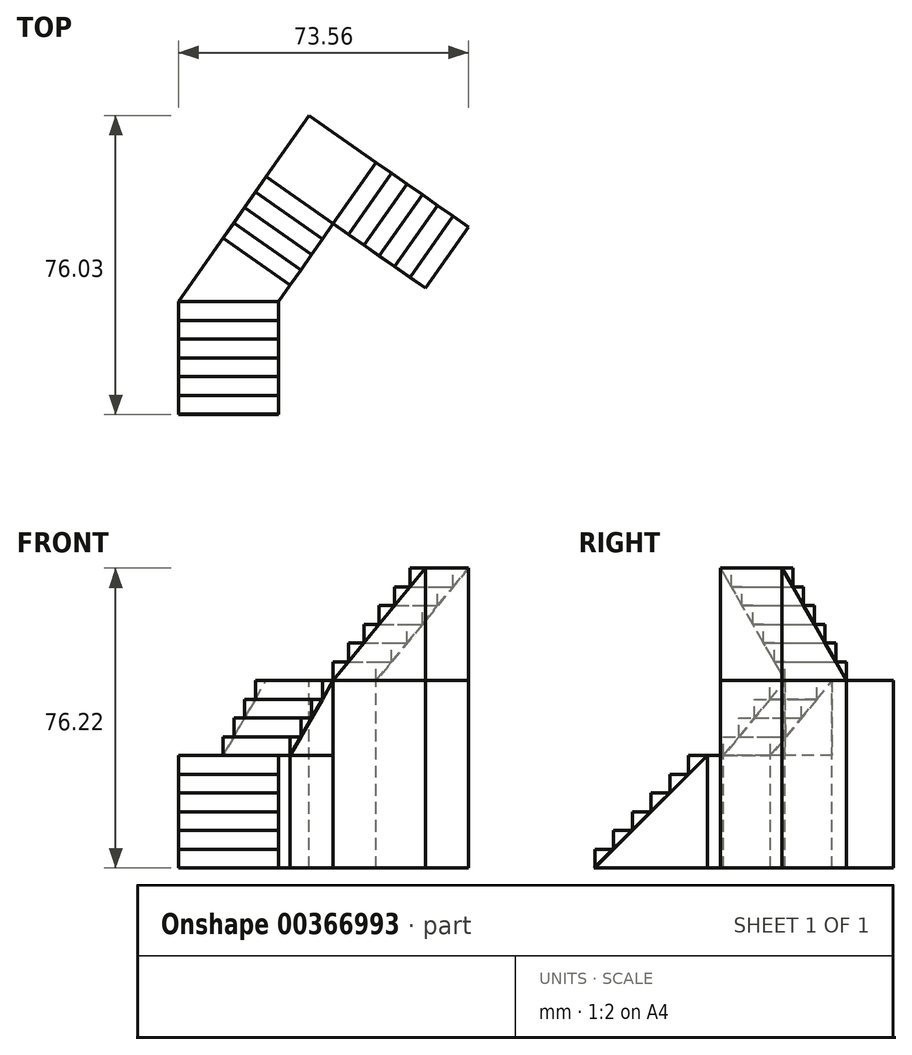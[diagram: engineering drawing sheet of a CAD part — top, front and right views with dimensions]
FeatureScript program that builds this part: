
annotation { "Feature Type Name" : "Feature", "Feature Type Description" : "" }
export const myFeature = defineFeature(function(context is Context, id is Id, definition is map)
    precondition{}
    {
        {
            var Q0;
            Q0=qCreatedBy(makeId("Right.planeOp"),FACE);
            var sketch = newSketch(context, id + "F0", { "sketchPlane" : qUnion([Q0])});
            skLineSegment(sketch, "E0", {"start": v(-19.36, -10.94) * mm, "end": v(9.22, 17.63) * mm});
            skLineSegment(sketch, "E1", {"start": v(-19.36, -10.94) * mm, "end": v(-19.36, -6.18) * mm});
            skLineSegment(sketch, "E2", {"start": v(-19.36, -6.18) * mm, "end": v(-14.6, -6.18) * mm});
            skLineSegment(sketch, "E3", {"start": v(-19.36, -10.94) * mm, "end": v(28.85, -10.94) * mm});
            skLineSegment(sketch, "E4", {"start": v(-14.6, -6.18) * mm, "end": v(-14.6, -1.42) * mm});
            skLineSegment(sketch, "E5", {"start": v(-14.6, -1.42) * mm, "end": v(-9.83, -1.42) * mm});
            skLineSegment(sketch, "E6", {"start": v(-9.83, -1.42) * mm, "end": v(-9.83, 3.35) * mm});
            skLineSegment(sketch, "E7", {"start": v(-9.83, 3.35) * mm, "end": v(-5.07, 3.35) * mm});
            skLineSegment(sketch, "E8", {"start": v(-5.07, 3.35) * mm, "end": v(-5.07, 8.1) * mm});
            skLineSegment(sketch, "E9", {"start": v(-5.07, 8.1) * mm, "end": v(-0.3, 8.1) * mm});
            skLineSegment(sketch, "E10", {"start": v(-0.3, 8.1) * mm, "end": v(-0.3, 12.87) * mm});
            skLineSegment(sketch, "E11", {"start": v(-0.3, 12.87) * mm, "end": v(4.45, 12.87) * mm});
            skLineSegment(sketch, "E12", {"start": v(4.45, 12.87) * mm, "end": v(4.45, 17.63) * mm});
            skLineSegment(sketch, "E13", {"start": v(4.45, 17.63) * mm, "end": v(9.22, 17.63) * mm});
            skSolve(sketch);
        }
        {
            var Q0;
            {var subQ2=sQuery(id+"F0.wireOp",EDGE,"E12");Q0=makeQuery(id+"F0.imprint","IMPRINT",FACE,{"disambiguationData":[TD([[makeQuery(id+"F0.imprint","IMPRINT",EDGE,{"derivedFrom":subQ2}),-1.0]])]});}
            var Q1;
            {var subQ0=sQuery(id+"F0.wireOp",EDGE,"E10");Q1=makeQuery(id+"F0.imprint","IMPRINT",FACE,{"disambiguationData":[TD([[makeQuery(id+"F0.imprint","IMPRINT",EDGE,{"derivedFrom":subQ0}),-1.0]])]});}
            var Q2;
            {var subQ0=sQuery(id+"F0.wireOp",EDGE,"E8");Q2=makeQuery(id+"F0.imprint","IMPRINT",FACE,{"disambiguationData":[TD([[makeQuery(id+"F0.imprint","IMPRINT",EDGE,{"derivedFrom":subQ0}),-1.0]])]});}
            var Q3;
            {var subQ0=sQuery(id+"F0.wireOp",EDGE,"E6");Q3=makeQuery(id+"F0.imprint","IMPRINT",FACE,{"disambiguationData":[TD([[makeQuery(id+"F0.imprint","IMPRINT",EDGE,{"derivedFrom":subQ0}),-1.0]])]});}
            var Q4;
            {var subQ0=sQuery(id+"F0.wireOp",EDGE,"E4");Q4=makeQuery(id+"F0.imprint","IMPRINT",FACE,{"disambiguationData":[TD([[makeQuery(id+"F0.imprint","IMPRINT",EDGE,{"derivedFrom":subQ0}),-1.0]])]});}
            var Q5;
            {var subQ0=sQuery(id+"F0.wireOp",EDGE,"E1");Q5=makeQuery(id+"F0.imprint","IMPRINT",FACE,{"disambiguationData":[TD([[makeQuery(id+"F0.imprint","IMPRINT",EDGE,{"derivedFrom":subQ0}),-1.0]])]});}
            extrude(context, id + "F1", {"entities" : qUnion([Q0, Q1, Q2, Q3, Q4, Q5]), "depth" : 25.4 * mm});
        }
        {
            var Q0;
            Q0=makeQuery(id+"F1.opExtrude","SWEPT_FACE",FACE,{"disambiguationData":[OSD([sQuery(id+"F0.wireOp",EDGE,"E13")])]});
            var sketch = newSketch(context, id + "F2", { "sketchPlane" : qUnion([Q0])});
            skLineSegment(sketch, "E14", {"start": v(0, 9.22) * mm, "end": v(11.27, 25.31) * mm});
            skLineSegment(sketch, "E15", {"start": v(25.4, 9.22) * mm, "end": v(28.31, 13.38) * mm});
            skLineSegment(sketch, "E16", {"start": v(28.31, 13.38) * mm, "end": v(11.27, 25.31) * mm});
            skSolve(sketch);
        }
        {
            var Q0;
            Q0=makeQuery(id+"F2.imprint","IMPRINT",FACE,{"disambiguationData":[TD([[makeQuery(id+"F2.imprint","IMPRINT",EDGE,{"derivedFrom":sQuery(id+"F2.wireOp",EDGE,"E14")}),-1.0]])]});
            extrude(context, id + "F3", {"entities" : qUnion([Q0]), "oppositeDirection" : true, "depth" : 28.57 * mm});
        }
        {
            var Q0;
            Q0=makeQuery(id+"F3.opExtrude","SWEPT_FACE",FACE,{"disambiguationData":[OSD([sQuery(id+"F2.wireOp",EDGE,"E14")])]});
            var sketch = newSketch(context, id + "F4", { "sketchPlane" : qUnion([Q0])});
            skLineSegment(sketch, "E17", {"start": v(-27.2, 17.64) * mm, "end": v(-46.25, 36.69) * mm});
            skLineSegment(sketch, "E18", {"start": v(-27.2, 17.64) * mm, "end": v(-27.2, 22.4) * mm});
            skLineSegment(sketch, "E19", {"start": v(-27.2, 22.4) * mm, "end": v(-31.96, 22.4) * mm});
            skLineSegment(sketch, "E20", {"start": v(-31.96, 22.4) * mm, "end": v(-31.96, 27.16) * mm});
            skLineSegment(sketch, "E21", {"start": v(-31.96, 27.16) * mm, "end": v(-36.72, 27.16) * mm});
            skLineSegment(sketch, "E22", {"start": v(-36.72, 27.16) * mm, "end": v(-36.72, 31.92) * mm});
            skLineSegment(sketch, "E23", {"start": v(-36.72, 31.92) * mm, "end": v(-41.48, 31.92) * mm});
            skLineSegment(sketch, "E24", {"start": v(-41.48, 31.92) * mm, "end": v(-41.48, 36.69) * mm});
            skLineSegment(sketch, "E25", {"start": v(-41.48, 36.69) * mm, "end": v(-46.25, 36.69) * mm});
            skSolve(sketch);
        }
        {
            var Q0;
            {var subQ0=sQuery(id+"F4.wireOp",EDGE,"E20");Q0=makeQuery(id+"F4.imprint","IMPRINT",FACE,{"disambiguationData":[TD([[makeQuery(id+"F4.imprint","IMPRINT",EDGE,{"derivedFrom":subQ0}),1.0]])]});}
            var Q1;
            {var subQ0=sQuery(id+"F4.wireOp",EDGE,"E18");Q1=makeQuery(id+"F4.imprint","IMPRINT",FACE,{"disambiguationData":[TD([[makeQuery(id+"F4.imprint","IMPRINT",EDGE,{"derivedFrom":subQ0}),1.0]])]});}
            var Q2;
            {var subQ0=sQuery(id+"F4.wireOp",EDGE,"E22");Q2=makeQuery(id+"F4.imprint","IMPRINT",FACE,{"disambiguationData":[TD([[makeQuery(id+"F4.imprint","IMPRINT",EDGE,{"derivedFrom":subQ0}),1.0]])]});}
            var Q3;
            {var subQ2=sQuery(id+"F4.wireOp",EDGE,"E24");Q3=makeQuery(id+"F4.imprint","IMPRINT",FACE,{"disambiguationData":[TD([[makeQuery(id+"F4.imprint","IMPRINT",EDGE,{"derivedFrom":subQ2}),1.0]])]});}
            extrude(context, id + "F5", {"entities" : qUnion([Q0, Q1, Q2, Q3]), "oppositeDirection" : true, "depth" : 20.8 * mm});
        }
        {
            var Q0;
            Q0=makeQuery(id+"F5.opExtrude","SWEPT_FACE",FACE,{"disambiguationData":[OSD([sQuery(id+"F4.wireOp",EDGE,"E25")])]});
            var sketch = newSketch(context, id + "F6", { "sketchPlane" : qUnion([Q0])});
            skLineSegment(sketch, "E26", {"start": v(22.2, 40.92) * mm, "end": v(33.12, 56.52) * mm});
            skLineSegment(sketch, "E27", {"start": v(39.24, 28.98) * mm, "end": v(50.17, 44.59) * mm});
            skLineSegment(sketch, "E28", {"start": v(33.12, 56.52) * mm, "end": v(50.17, 44.59) * mm});
            skLineSegment(sketch, "E29", {"start": v(22.2, 40.92) * mm, "end": v(39.24, 28.98) * mm});
            skSolve(sketch);
        }
        {
            var Q0;
            Q0=makeQuery(id+"F6.imprint","IMPRINT",FACE,{"disambiguationData":[TD([[makeQuery(id+"F6.imprint","IMPRINT",EDGE,{"derivedFrom":sQuery(id+"F6.wireOp",EDGE,"E26")}),-1.0]])]});
            extrude(context, id + "F7", {"entities" : qUnion([Q0]), "oppositeDirection" : true, "depth" : 47.62 * mm});
        }
        {
            var Q0;
            Q0=makeQuery(id+"F7.opExtrude","SWEPT_FACE",FACE,{"disambiguationData":[OSD([sQuery(id+"F6.wireOp",EDGE,"E28")])]});
            var sketch = newSketch(context, id + "F8", { "sketchPlane" : qUnion([Q0])});
            skLineSegment(sketch, "E30", {"start": v(-15.52, 36.68) * mm, "end": v(-44.08, 65.24) * mm});
            skLineSegment(sketch, "E31", {"start": v(-15.52, 36.68) * mm, "end": v(-15.52, 41.45) * mm});
            skLineSegment(sketch, "E32", {"start": v(-15.52, 41.45) * mm, "end": v(-20.28, 41.45) * mm});
            skLineSegment(sketch, "E33", {"start": v(-20.28, 41.45) * mm, "end": v(-20.28, 46.2) * mm});
            skLineSegment(sketch, "E34", {"start": v(-20.28, 46.2) * mm, "end": v(-25.05, 46.2) * mm});
            skLineSegment(sketch, "E35", {"start": v(-25.05, 46.2) * mm, "end": v(-25.05, 50.97) * mm});
            skLineSegment(sketch, "E36", {"start": v(-25.05, 50.97) * mm, "end": v(-29.81, 50.97) * mm});
            skLineSegment(sketch, "E37", {"start": v(-29.81, 50.97) * mm, "end": v(-29.81, 55.73) * mm});
            skLineSegment(sketch, "E38", {"start": v(-29.81, 55.73) * mm, "end": v(-34.57, 55.73) * mm});
            skLineSegment(sketch, "E39", {"start": v(-34.57, 55.73) * mm, "end": v(-34.57, 60.5) * mm});
            skLineSegment(sketch, "E40", {"start": v(-34.57, 60.5) * mm, "end": v(-39.34, 60.5) * mm});
            skLineSegment(sketch, "E41", {"start": v(-39.34, 60.5) * mm, "end": v(-39.34, 65.26) * mm});
            skLineSegment(sketch, "E42", {"start": v(-39.34, 65.26) * mm, "end": v(-44.08, 65.24) * mm});
            skSolve(sketch);
        }
        {
            var Q0;
            {var subQ2=sQuery(id+"F8.wireOp",EDGE,"E41");Q0=makeQuery(id+"F8.imprint","IMPRINT",FACE,{"disambiguationData":[TD([[makeQuery(id+"F8.imprint","IMPRINT",EDGE,{"derivedFrom":subQ2}),1.0]])]});}
            var Q1;
            {var subQ0=sQuery(id+"F8.wireOp",EDGE,"E39");Q1=makeQuery(id+"F8.imprint","IMPRINT",FACE,{"disambiguationData":[TD([[makeQuery(id+"F8.imprint","IMPRINT",EDGE,{"derivedFrom":subQ0}),1.0]])]});}
            var Q2;
            {var subQ0=sQuery(id+"F8.wireOp",EDGE,"E37");Q2=makeQuery(id+"F8.imprint","IMPRINT",FACE,{"disambiguationData":[TD([[makeQuery(id+"F8.imprint","IMPRINT",EDGE,{"derivedFrom":subQ0}),1.0]])]});}
            var Q3;
            {var subQ0=sQuery(id+"F8.wireOp",EDGE,"E35");Q3=makeQuery(id+"F8.imprint","IMPRINT",FACE,{"disambiguationData":[TD([[makeQuery(id+"F8.imprint","IMPRINT",EDGE,{"derivedFrom":subQ0}),1.0]])]});}
            var Q4;
            {var subQ0=sQuery(id+"F8.wireOp",EDGE,"E33");Q4=makeQuery(id+"F8.imprint","IMPRINT",FACE,{"disambiguationData":[TD([[makeQuery(id+"F8.imprint","IMPRINT",EDGE,{"derivedFrom":subQ0}),1.0]])]});}
            var Q5;
            {var subQ0=sQuery(id+"F8.wireOp",EDGE,"E31");Q5=makeQuery(id+"F8.imprint","IMPRINT",FACE,{"disambiguationData":[TD([[makeQuery(id+"F8.imprint","IMPRINT",EDGE,{"derivedFrom":subQ0}),1.0]])]});}
            extrude(context, id + "F9", {"entities" : qUnion([Q0, Q1, Q2, Q3, Q4, Q5]), "oppositeDirection" : true, "depth" : 19.05 * mm});
        }
        {
            var Q0;
            Q0=makeQuery(id+"F1.opExtrude","CAP_FACE",FACE,{"disambiguationData":[OSD([sQuery(id+"F0.wireOp",EDGE,"E0"),sQuery(id+"F0.wireOp",EDGE,"E12"),sQuery(id+"F0.wireOp",EDGE,"E13")])],"isStart":false});
            var sketch = newSketch(context, id + "F10", { "sketchPlane" : qUnion([Q0])});
            skLineSegment(sketch, "E43", {"start": v(9.22, 17.63) * mm, "end": v(9.22, -10.94) * mm});
            skLineSegment(sketch, "E44", {"start": v(9.22, -10.94) * mm, "end": v(-19.51, -10.94) * mm});
            skLineSegment(sketch, "E45", {"start": v(-19.51, -10.94) * mm, "end": v(9.22, 17.63) * mm});
            skSolve(sketch);
        }
        {
            var Q0;
            Q0=makeQuery(id+"F10.imprint","IMPRINT",FACE,{"disambiguationData":[TD([[makeQuery(id+"F10.imprint","IMPRINT",EDGE,{"derivedFrom":sQuery(id+"F10.wireOp",EDGE,"E43")}),-1.0]])]});
            extrude(context, id + "F11", {"entities" : qUnion([Q0]), "oppositeDirection" : true, "depth" : 25.4 * mm});
        }
        {
            var Q0;
            Q0=makeQuery(id+"F5.opExtrude","CAP_FACE",FACE,{"disambiguationData":[OSD([sQuery(id+"F4.wireOp",EDGE,"E17"),sQuery(id+"F4.wireOp",EDGE,"E24"),sQuery(id+"F4.wireOp",EDGE,"E25")])],"isStart":false});
            var sketch = newSketch(context, id + "F12", { "sketchPlane" : qUnion([Q0])});
            skLineSegment(sketch, "E46", {"start": v(46.25, 36.69) * mm, "end": v(46.25, 17.64) * mm});
            skLineSegment(sketch, "E47", {"start": v(46.25, 17.64) * mm, "end": v(27.2, 17.64) * mm});
            skLineSegment(sketch, "E48", {"start": v(46.25, 36.69) * mm, "end": v(27.2, 17.64) * mm});
            skSolve(sketch);
        }
        {
            var Q0;
            Q0=makeQuery(id+"F12.imprint","IMPRINT",FACE,{"disambiguationData":[TD([[makeQuery(id+"F12.imprint","IMPRINT",EDGE,{"derivedFrom":sQuery(id+"F12.wireOp",EDGE,"E46")}),-1.0]])]});
            extrude(context, id + "F13", {"entities" : qUnion([Q0]), "oppositeDirection" : true, "depth" : 20.8 * mm});
        }
        {
            var Q0;
            Q0=makeQuery(id+"F9.opExtrude","CAP_FACE",FACE,{"disambiguationData":[OSD([sQuery(id+"F8.wireOp",EDGE,"E30"),sQuery(id+"F8.wireOp",EDGE,"E41"),sQuery(id+"F8.wireOp",EDGE,"E42")])],"isStart":false});
            var sketch = newSketch(context, id + "F14", { "sketchPlane" : qUnion([Q0])});
            skLineSegment(sketch, "E49", {"start": v(44.08, 65.24) * mm, "end": v(44.08, 36.67) * mm});
            skLineSegment(sketch, "E50", {"start": v(44.08, 36.67) * mm, "end": v(15.5, 36.67) * mm});
            skLineSegment(sketch, "E51", {"start": v(44.08, 65.24) * mm, "end": v(15.5, 36.67) * mm});
            skSolve(sketch);
        }
        {
            var Q0;
            Q0=makeQuery(id+"F14.imprint","IMPRINT",FACE,{"disambiguationData":[TD([[makeQuery(id+"F14.imprint","IMPRINT",EDGE,{"derivedFrom":sQuery(id+"F14.wireOp",EDGE,"E49")}),-1.0]])]});
            extrude(context, id + "F15", {"entities" : qUnion([Q0]), "oppositeDirection" : true, "depth" : 19.05 * mm});
        }
        {
            var Q0;
            Q0=makeQuery(id+"F15.opExtrude","SWEPT_FACE",FACE,{"disambiguationData":[OSD([sQuery(id+"F14.wireOp",EDGE,"E50")])]});
            var sketch = newSketch(context, id + "F16", { "sketchPlane" : qUnion([Q0])});
            skLineSegment(sketch, "E52", {"start": v(73.56, -28.2) * mm, "end": v(50.15, -44.6) * mm});
            skLineSegment(sketch, "E53", {"start": v(50.15, -44.6) * mm, "end": v(39.23, -28.99) * mm});
            skLineSegment(sketch, "E54", {"start": v(39.23, -28.99) * mm, "end": v(62.63, -12.6) * mm});
            skLineSegment(sketch, "E55", {"start": v(62.63, -12.6) * mm, "end": v(73.56, -28.2) * mm});
            skSolve(sketch);
        }
        {
            var Q0;
            Q0=makeQuery(id+"F16.imprint","IMPRINT",FACE,{"disambiguationData":[TD([[makeQuery(id+"F16.imprint","IMPRINT",EDGE,{"derivedFrom":sQuery(id+"F16.wireOp",EDGE,"E52")}),-1.0]])]});
            extrude(context, id + "F17", {"entities" : qUnion([Q0]), "depth" : 47.62 * mm});
        }
        {
            var Q0;
            Q0=makeQuery(id+"F13.opExtrude","SWEPT_FACE",FACE,{"disambiguationData":[OSD([sQuery(id+"F12.wireOp",EDGE,"E47")])]});
            var sketch = newSketch(context, id + "F18", { "sketchPlane" : qUnion([Q0])});
            skLineSegment(sketch, "E56", {"start": v(22.2, -40.92) * mm, "end": v(11.27, -25.31) * mm});
            skLineSegment(sketch, "E57", {"start": v(11.27, -25.31) * mm, "end": v(28.31, -13.38) * mm});
            skLineSegment(sketch, "E58", {"start": v(28.31, -13.38) * mm, "end": v(39.24, -28.98) * mm});
            skLineSegment(sketch, "E59", {"start": v(39.24, -28.98) * mm, "end": v(22.2, -40.92) * mm});
            skSolve(sketch);
        }
        {
            var Q0;
            Q0=makeQuery(id+"F18.imprint","IMPRINT",FACE,{"disambiguationData":[TD([[makeQuery(id+"F18.imprint","IMPRINT",EDGE,{"derivedFrom":sQuery(id+"F18.wireOp",EDGE,"E56")}),-1.0]])]});
            extrude(context, id + "F19", {"entities" : qUnion([Q0]), "depth" : 28.57 * mm});
        }
    });
